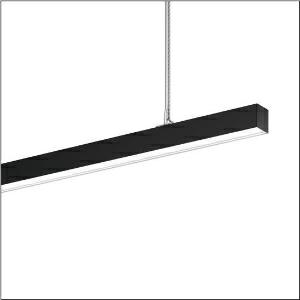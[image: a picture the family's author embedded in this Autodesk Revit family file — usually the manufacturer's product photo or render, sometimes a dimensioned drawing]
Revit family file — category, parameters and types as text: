
# Revit family: silica_r__21_51mx33dc4dbb_4870
name_source: partatom
category: Lighting Fixtures
units: mm (PartAtom-declared; Revit-internal decimal feet)

## family parameters
Cut with Voids When Loaded = No
Host = Face
Light Source = No
Part Type = Normal
Room Calculation Point = No
Round Connector Dimension = Use Diameter
Shared = No

## types (1)
- --- (1 x LED, 14790 lm, 93.9 W, 4000K)
    Apparent Load = 94 VA
    CIE Flux Codes = 78 96 99 55 100
    Color Rendering = 80
    Color Temperature = 4000K
    Default Elevation = 1800 mm
    Description = Silica® 21, office luminaire, primary optical cover: prismatic diffuser, of PMMA, CAT 2 (L<= 3000cd/m²), light emission: direct/indirect distribution, primary light characteristic: symmetric, installation type: suspended mounting, LED, rated luminous flux: 14.790lm, luminous efficacy: 158lm/W, light colour: 840, colour temperature: 4000K, with terminal, 3+2-pole, max. 2.5mm², mains connection: 220..240V, AC, 50/60Hz, rated input power: 93.9W, luminaire housing, of aluminium, jet black (RAL 9005), length: 3.004mm, width: 53mm, height: 53mm, protection rating (complete): IP20, insulation class (complete): insulation class I (protective earthing), certification: CE, permissible operating ambient temperature: 0..+35°C, standard: EN 50419, packaging unit: 1 piece
    Height = 53 mm
    Lamp = 1 x LED
    Lamp Light Flux = 14790 lm
    Lamp Power = 93.9 W
    Lamp count = 1
    Length = 3004 mm
    Luminous efficacy = 158 lm/W
    Manufacturer = Siteco
    ModVariant = No
    Model = 51MX33DC4DBB
    Mounting Place = Ceiling
    Mounting Type = Pendant
    Number of Poles = 1
    OnlyDefault = Yes
    Power Factor = 1
    Product Name = Silica® 21
    Product group = office luminaire | ceiling pendant
    ProductGroupID = 902
    Protection Class = Protection class I
    Protection Degree = IP 20
    RLX_Detail_Level = 1
    RLX_Emergency_Light_Flux = 0 lm
    RLX_Emergency_Type = 0
    RLX_Emergency_Type_DB = No
    RlxData = <blob elided: 26121 chars, md5=7f172e21>
    Socket = socket
    Standby Power = 0 W
    System Light Flux = 14790 lm
    System Power = 94 W
    Type Comments = factory setting: luminous flux: 100 % | dim-lin: 254 | 323 mA
    Type Image = l_1335856.jpg
    URL = http://relux.com
    VarID = @adj_087837
    Voltage = 0 V
    Weight = 0.00 kg
    Width = 53 mm

## geometry (parser evidence)
native form markers: Blend x4, Sweep x11
no freeform markers — native parametric forms only
